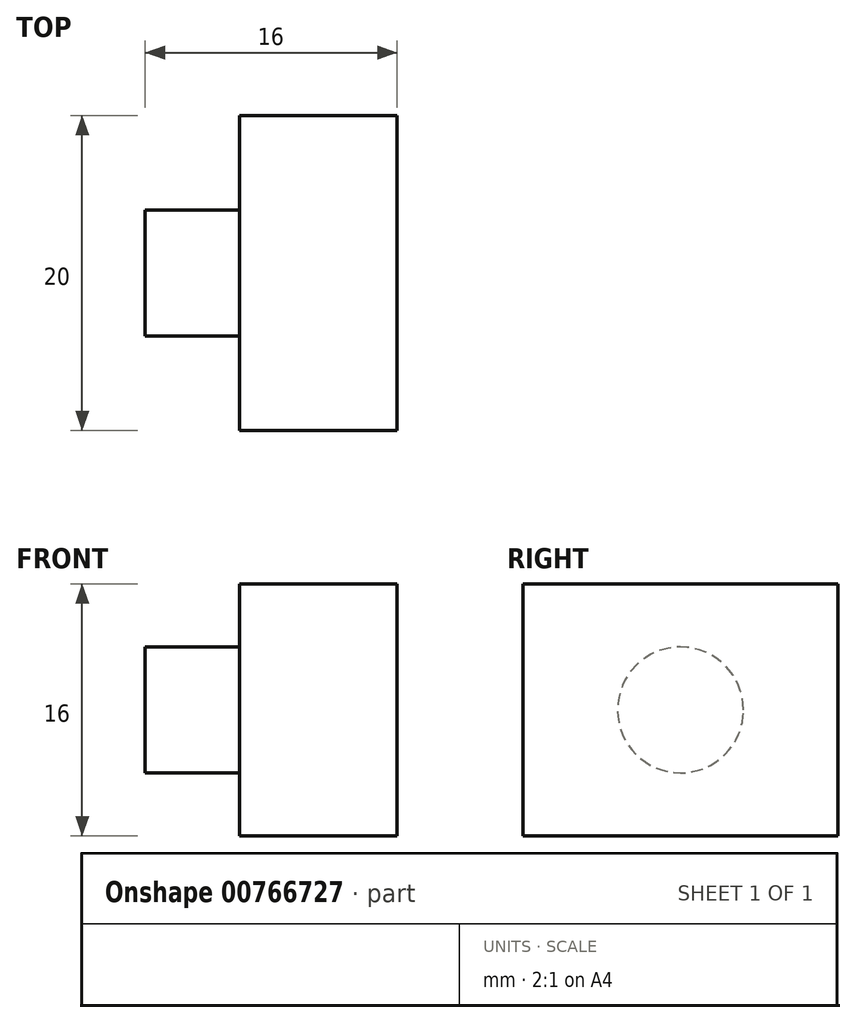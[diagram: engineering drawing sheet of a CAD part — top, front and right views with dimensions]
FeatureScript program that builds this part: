
annotation { "Feature Type Name" : "Feature", "Feature Type Description" : "" }
export const myFeature = defineFeature(function(context is Context, id is Id, definition is map)
    precondition{}
    {
        {
            var Q0;
            Q0=qCreatedBy(makeId("Top.planeOp"),FACE);
            var sketch = newSketch(context, id + "F0", { "sketchPlane" : qUnion([Q0])});
            skLineSegment(sketch, "E0.bottom", {"start": v(5, 10) * mm, "end": v(-5, 10) * mm});
            skLineSegment(sketch, "E0.top", {"start": v(5, -10) * mm, "end": v(-5, -10) * mm});
            skLineSegment(sketch, "E0.left", {"start": v(5, 10) * mm, "end": v(5, -10) * mm});
            skLineSegment(sketch, "E0.right", {"start": v(-5, 10) * mm, "end": v(-5, -10) * mm});
            skPoint(sketch, "E0.middle", {"position": v(0, 0) * mm});
            skSolve(sketch);
        }
        {
            var Q0;
            Q0 = qSketchRegion(id + "F0", true);
            extrude(context, id + "F1", {"entities" : qUnion([Q0]), "depth" : 16 * mm, "offsetDistance" : 25 * mm});
        }
        {
            var Q0;
            Q0=makeQuery(id+"F1.opExtrude","SWEPT_FACE",FACE,{"disambiguationData":[OSD([sQuery(id+"F0.wireOp",EDGE,"E0.right")])]});
            var sketch = newSketch(context, id + "F2", { "sketchPlane" : qUnion([Q0])});
            skCircle(sketch, "E1", {"center": v(0, 8) * mm, "radius": 4 * mm});
            skSolve(sketch);
        }
        {
            var Q0;
            Q0 = qSketchRegion(id + "F2", true);
            extrude(context, id + "F3", {"entities" : qUnion([Q0]), "operationType" : NewBodyOperationType.ADD, "depth" : 6 * mm, "offsetDistance" : 25 * mm});
        }
    });
